# Revit family: YGNIS_Caldera de condensación LR
name_source: partatom
category: Equipos mecánicos
revit_build: Autodesk Revit 2016 (Build: 20150220_1215(x64)
units: mm (PartAtom-declared; Revit-internal decimal feet)

## family parameters
Compartido = No
Corte con vacíos al cargar = No
Cota de conector redondo = Diámetro de uso
Número OmniClass = 23.75.00.00
Punto de cálculo de habitación = No
Se basa en plano de trabajo = No
Siempre vertical = Sí
Tipo de pieza = Normal
Título OmniClass = Climate Control (HVAC)

## types (6) — shared parameters
Código de montaje = D3020100
Descripción = Caldera de condensación con juego de turbuladores para los tubos de humos, para equipar con quemador presurizado de gas o gasóleo, homologada como baja temperatura según directiva 92/42 CE
Fabricante = YGNIS Atlantic
Presión de servicio = 5.9 atm
URL = http://www.ygnis.es
a = 145 mm  [stored 0.475722 ft]

## per-type parameters (varying)
| type | B | H | L | Peso | Potencia útil | Volumen | Volumen de gas | b | c | d1 | d2 | e | e. ext | e. int | f | g | h | i | j | k | l | ø empalme ida-retorno |
| LR 23 | 1180 mm  [stored 3.87139 ft] | 1450 mm | 2240 mm | 1490.00 kg | 630 kW | 650.0 L | 690.0 L | 1060 mm  [stored 3.47769 ft] | 300 mm | 690 mm | 1000 mm  [stored 3.28084 ft] | 250 mm  [stored 0.82021 ft] | 325 mm  [stored 1.06627 ft] | 245 mm  [stored 0.803806 ft] | 100 mm  [stored 0.328084 ft] | 100 mm  [stored 0.328084 ft] | 1370 mm  [stored 4.49475 ft] | 150 mm | 950 mm  [stored 3.1168 ft] | 100 mm  [stored 0.328084 ft] | 1695 mm | 200 mm  [stored 0.656168 ft] |
| LR 24 | 1250 mm  [stored 4.10105 ft] | 1535 mm | 2460 mm | 1810.00 kg | 700 kW | 790.0 L | 910.0 L | 1130 mm  [stored 3.70735 ft] | 335 mm  [stored 1.09908 ft] | 740 mm  [stored 2.42782 ft] | 1055 mm  [stored 3.46129 ft] | 250 mm  [stored 0.82021 ft] | 325 mm  [stored 1.06627 ft] | 245 mm  [stored 0.803806 ft] | 100 mm  [stored 0.328084 ft] | 100 mm  [stored 0.328084 ft] | 1455 mm | 200 mm  [stored 0.656168 ft] | 1150 mm | 115 mm  [stored 0.377297 ft] | 1880 mm | 200 mm  [stored 0.656168 ft] |
| LR 25 | 1250 mm  [stored 4.10105 ft] | 1535 mm | 2460 mm | 1810.00 kg | 800 kW | 790.0 L | 910.0 L | 1130 mm  [stored 3.70735 ft] | 335 mm  [stored 1.09908 ft] | 740 mm  [stored 2.42782 ft] | 1055 mm  [stored 3.46129 ft] | 250 mm  [stored 0.82021 ft] | 325 mm  [stored 1.06627 ft] | 245 mm  [stored 0.803806 ft] | 100 mm  [stored 0.328084 ft] | 100 mm  [stored 0.328084 ft] | 1455 mm | 200 mm  [stored 0.656168 ft] | 1150 mm | 115 mm  [stored 0.377297 ft] | 1880 mm | 200 mm  [stored 0.656168 ft] |
| LR 26 | 1330 mm  [stored 4.36352 ft] | 1625 mm | 2565 mm | 2000.00 kg | 895 kW | 960.0 L | 1100.0 L | 1210 mm  [stored 3.96982 ft] | 345 mm  [stored 1.13189 ft] | 790 mm  [stored 2.59186 ft] | 1115 mm  [stored 3.65814 ft] | 300 mm | 375 mm  [stored 1.23031 ft] | 295 mm  [stored 0.967848 ft] | 100 mm  [stored 0.328084 ft] | 100 mm  [stored 0.328084 ft] | 1545 mm | 200 mm  [stored 0.656168 ft] | 1150 mm | 125 mm  [stored 0.410105 ft] | 1975 mm | 200 mm  [stored 0.656168 ft] |
| LR 27 | 1420 mm | 1730 mm | 2939 mm | 2460.00 kg | 1150 kW | 1360.0 L | 1460.0 L | 1300 mm  [stored 4.26509 ft] | 400 mm  [stored 1.31234 ft] | 840 mm  [stored 2.75591 ft] | 1200 mm | 350 mm  [stored 1.14829 ft] | 425 mm  [stored 1.39436 ft] | 345 mm  [stored 1.13189 ft] | 80 mm  [stored 0.262467 ft] | 125 mm  [stored 0.410105 ft] | 1650 mm | 238 mm  [stored 0.78084 ft] | 1493 mm | 110 mm  [stored 0.360892 ft] | 2314 mm | 225 mm  [stored 0.738189 ft] |
| LR 28 | 1420 mm | 1730 mm | 2939 mm | 2460.00 kg | 1300 kW | 1360.0 L | 1460.0 L | 1300 mm  [stored 4.26509 ft] | 400 mm  [stored 1.31234 ft] | 840 mm  [stored 2.75591 ft] | 1200 mm | 350 mm  [stored 1.14829 ft] | 425 mm  [stored 1.39436 ft] | 345 mm  [stored 1.13189 ft] | 80 mm  [stored 0.262467 ft] | 125 mm  [stored 0.410105 ft] | 1650 mm | 238 mm  [stored 0.78084 ft] | 1493 mm | 110 mm  [stored 0.360892 ft] | 2314 mm | 225 mm  [stored 0.738189 ft] |

note: column(s) folded — value = type name in every type: Modelo

note: [stored X ft] marks values corroborated as IEEE doubles in the binary element streams (Revit-internal decimal feet)

## geometry (parser evidence)
native form markers: Blend x1
no freeform markers — native parametric forms only
